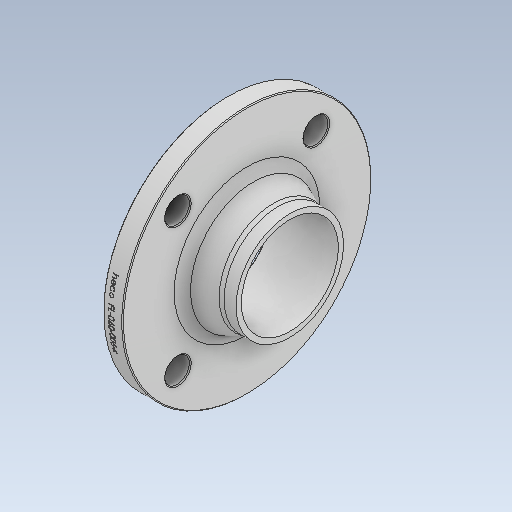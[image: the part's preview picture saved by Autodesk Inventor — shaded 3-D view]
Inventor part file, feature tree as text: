
AUTODESK INVENTOR PART (.ipt)
format: ipt  version: 2021 (Build 250183000, 183)  size: 480,256 bytes
history: imported  units: in
note: dims shown in document units (in); Inventor stores cm internally (conversion verified against a paired STEP export)
features: imported_body x1
ambient origin geometry x8: Origin, YZ Plane, XZ Plane, XY Plane, X Axis, Y Axis, Z Axis, Center Point
bodies: Solid1 (imported_parasolid), Body1 (imported_parasolid)
feature tree (1):
  imported_body  NMx_Import_Brep_tag  [imported B-rep: ~8 faces, bbox_mm=[0.0, 0.0, 0.0]]
